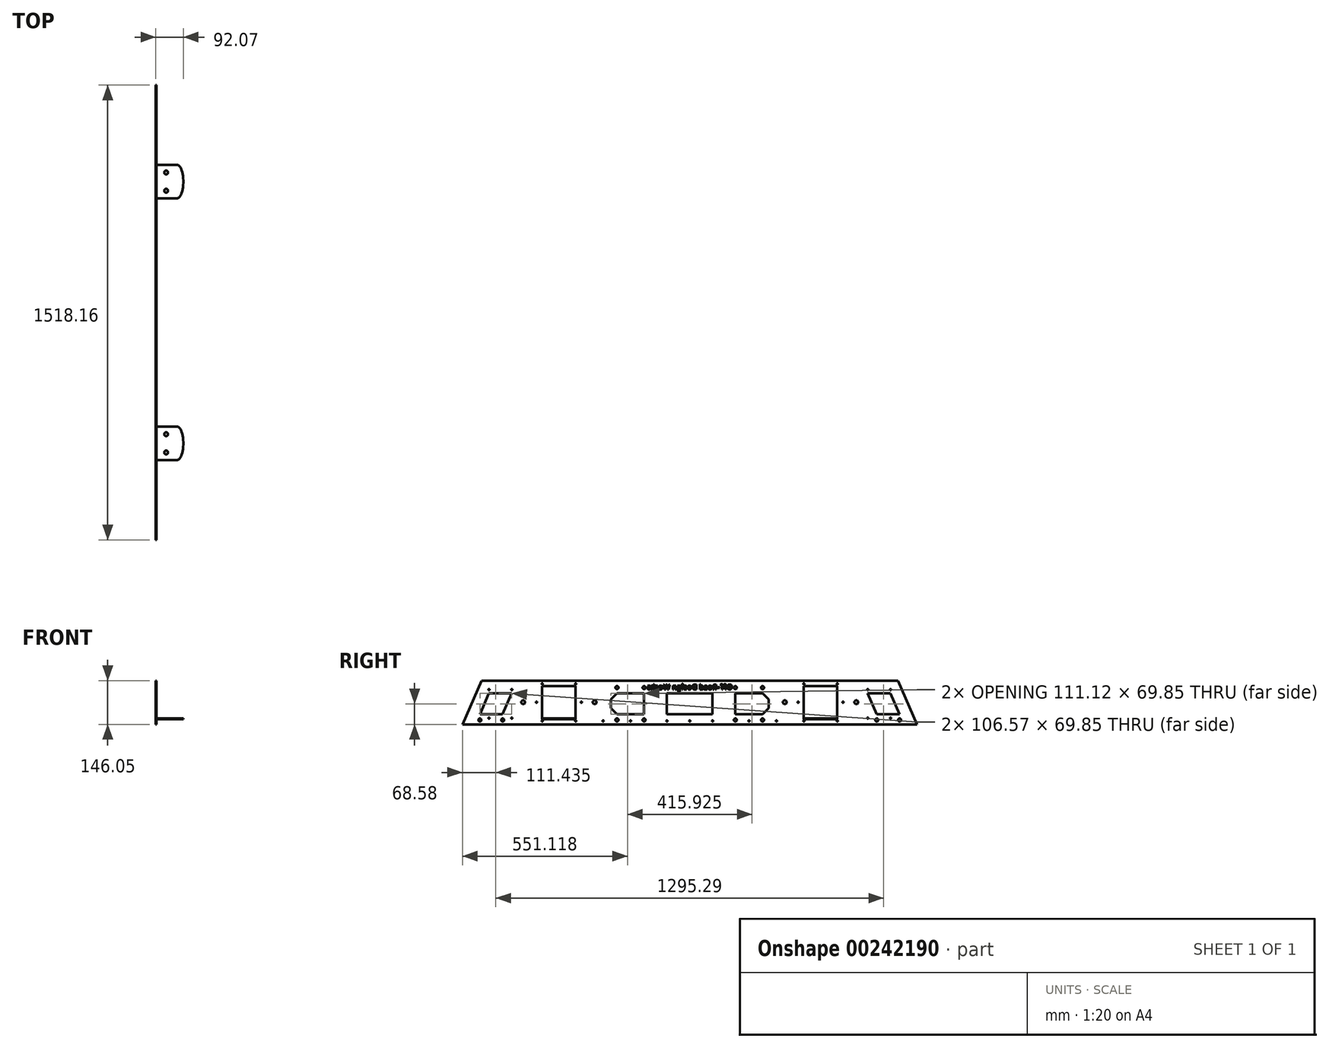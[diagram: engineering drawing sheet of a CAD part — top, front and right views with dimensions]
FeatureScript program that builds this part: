
annotation { "Feature Type Name" : "Feature", "Feature Type Description" : "" }
export const myFeature = defineFeature(function(context is Context, id is Id, definition is map)
    precondition{}
    {
        {
            var Q0;
            Q0=qCreatedBy(makeId("Right.planeOp"),FACE);
            var sketch = newSketch(context, id + "F0", { "sketchPlane" : qUnion([Q0])});
            skLineSegment(sketch, "E0", {"start": v(0, 0) * mm, "end": v(-759.08, 0) * mm});
            skLineSegment(sketch, "E1", {"start": v(-759.08, 0) * mm, "end": v(-695.58, 146.05) * mm});
            skLineSegment(sketch, "E2", {"start": v(-695.58, 146.05) * mm, "end": v(0, 146.05) * mm});
            skLineSegment(sketch, "E3", {"start": v(0, 0) * mm, "end": v(0, 460.36) * mm, "construction": true});
            skLineSegment(sketch, "E4.MirrorCS", {"start": v(695.58, 146.05) * mm, "end": v(0, 146.05) * mm});
            skLineSegment(sketch, "E5.MirrorCS", {"start": v(759.08, 0) * mm, "end": v(695.58, 146.05) * mm});
            skLineSegment(sketch, "E6.MirrorCS", {"start": v(0, 0) * mm, "end": v(759.08, 0) * mm});
            skSolve(sketch);
        }
        {
            var Q0;
            Q0=qSketchRegion(id+"F0",true);
            extrude(context, id + "F1", {"entities" : qUnion([Q0]), "oppositeDirection" : true, "depth" : 3.17 * mm});
        }
        {
            var Q0;
            Q0=makeQuery(id+"F1.opExtrude","CAP_FACE",FACE,{"disambiguationData":[OSD([sQuery(id+"F0.wireOp",EDGE,"E0"),sQuery(id+"F0.wireOp",EDGE,"E1"),sQuery(id+"F0.wireOp",EDGE,"E2"),sQuery(id+"F0.wireOp",EDGE,"E4.MirrorCS"),sQuery(id+"F0.wireOp",EDGE,"E5.MirrorCS"),sQuery(id+"F0.wireOp",EDGE,"E6.MirrorCS")])],"isStart":true});
            var sketch = newSketch(context, id + "F2", { "sketchPlane" : qUnion([Q0])});
            skLineSegment(sketch, "E7", {"start": v(0, 0) * mm, "end": v(0, 457.35) * mm, "construction": true});
            skLineSegment(sketch, "E8.bottom", {"start": v(-492.76, 127.5) * mm, "end": v(-381, 127.5) * mm});
            skLineSegment(sketch, "E8.top", {"start": v(-492.76, 20.32) * mm, "end": v(-381, 20.32) * mm});
            skLineSegment(sketch, "E8.left", {"start": v(-492.76, 127.5) * mm, "end": v(-492.76, 20.32) * mm});
            skLineSegment(sketch, "E8.right", {"start": v(-381, 127.5) * mm, "end": v(-381, 20.32) * mm});
            skLineSegment(sketch, "E9", {"start": v(-594.36, 103.5) * mm, "end": v(-670.56, 103.5) * mm});
            skLineSegment(sketch, "E10", {"start": v(-670.56, 103.5) * mm, "end": v(-700.93, 33.65) * mm});
            skLineSegment(sketch, "E11", {"start": v(-700.93, 33.65) * mm, "end": v(-624.73, 33.65) * mm});
            skLineSegment(sketch, "E12", {"start": v(-624.73, 33.65) * mm, "end": v(-594.36, 103.5) * mm});
            skArc(sketch, "E13.cCircle", {"start": v(-228.6, 103.5) * mm, "mid": v(-263.53, 68.58) * mm, "end": v(-228.6, 33.65) * mm, "construction": true});
            skLineSegment(sketch, "E13.0", {"start": v(-243.07, 103.5) * mm, "end": v(-214.13, 103.5) * mm});
            skLineSegment(sketch, "E13.4", {"start": v(-214.13, 33.65) * mm, "end": v(-243.07, 33.65) * mm});
            skLineSegment(sketch, "E13.5", {"start": v(-243.07, 33.65) * mm, "end": v(-263.53, 54.11) * mm});
            skLineSegment(sketch, "E13.6", {"start": v(-263.53, 54.11) * mm, "end": v(-263.53, 83.05) * mm});
            skLineSegment(sketch, "E13.7", {"start": v(-263.53, 83.05) * mm, "end": v(-243.07, 103.5) * mm});
            skPoint(sketch, "E13.0.midPoint", {"position": v(-228.6, 103.5) * mm});
            skLineSegment(sketch, "E14", {"start": v(-228.6, 33.65) * mm, "end": v(-152.4, 33.65) * mm});
            skLineSegment(sketch, "E15.MirrorCS", {"start": v(492.76, 127.5) * mm, "end": v(381, 127.5) * mm});
            skLineSegment(sketch, "E16.MirrorCS", {"start": v(492.76, 20.32) * mm, "end": v(381, 20.32) * mm});
            skLineSegment(sketch, "E17.MirrorCS", {"start": v(492.76, 127.5) * mm, "end": v(492.76, 20.32) * mm});
            skLineSegment(sketch, "E18.MirrorCS", {"start": v(381, 127.5) * mm, "end": v(381, 20.32) * mm});
            skLineSegment(sketch, "E19.MirrorCS", {"start": v(594.36, 103.5) * mm, "end": v(670.56, 103.5) * mm});
            skLineSegment(sketch, "E20.MirrorCS", {"start": v(670.56, 103.5) * mm, "end": v(700.93, 33.66) * mm});
            skLineSegment(sketch, "E21.MirrorCS", {"start": v(700.93, 33.65) * mm, "end": v(624.73, 33.65) * mm});
            skLineSegment(sketch, "E22.MirrorCS", {"start": v(624.73, 33.65) * mm, "end": v(594.36, 103.5) * mm});
            skLineSegment(sketch, "E23.MirrorCS", {"start": v(263.53, 54.11) * mm, "end": v(263.53, 83.05) * mm});
            skLineSegment(sketch, "E24.MirrorCS", {"start": v(263.53, 83.05) * mm, "end": v(243.07, 103.5) * mm});
            skArc(sketch, "E25.MirrorCS", {"start": v(228.6, 103.5) * mm, "mid": v(263.53, 68.58) * mm, "end": v(228.6, 33.65) * mm, "construction": true});
            skLineSegment(sketch, "E26.MirrorCS", {"start": v(243.07, 33.65) * mm, "end": v(263.53, 54.11) * mm});
            skLineSegment(sketch, "E27.MirrorCS", {"start": v(214.13, 33.65) * mm, "end": v(243.07, 33.65) * mm});
            skLineSegment(sketch, "E28.MirrorCS", {"start": v(243.07, 103.5) * mm, "end": v(214.13, 103.5) * mm});
            skLineSegment(sketch, "E29.MirrorCS", {"start": v(0, 103.5) * mm, "end": v(76.2, 103.5) * mm});
            skLineSegment(sketch, "E30.MirrorCS", {"start": v(228.6, 33.65) * mm, "end": v(152.4, 33.65) * mm});
            skLineSegment(sketch, "E31", {"start": v(-114.3, 103.5) * mm, "end": v(-114.3, -30.3) * mm, "construction": true});
            skLineSegment(sketch, "E32", {"start": v(-152.4, 103.5) * mm, "end": v(-152.4, 33.65) * mm});
            skLineSegment(sketch, "E33.MirrorCS", {"start": v(-76.2, 103.5) * mm, "end": v(-76.2, 33.65) * mm});
            skLineSegment(sketch, "E34.trimOffspring", {"start": v(-152.4, 103.5) * mm, "end": v(-228.6, 103.5) * mm});
            skPoint(sketch, "E35.start.orphan", {"position": v(0, 103.5) * mm});
            skLineSegment(sketch, "E36.trimOffspring", {"start": v(-76.2, 33.65) * mm, "end": v(0, 33.65) * mm});
            skLineSegment(sketch, "E37", {"start": v(-76.2, 103.5) * mm, "end": v(0, 103.5) * mm});
            skLineSegment(sketch, "E38", {"start": v(114.3, 103.5) * mm, "end": v(114.3, -63.26) * mm, "construction": true});
            skPoint(sketch, "E38.endSnap0", {"position": v(114.3, 103.5) * mm});
            skLineSegment(sketch, "E39", {"start": v(152.4, 103.5) * mm, "end": v(152.4, 33.65) * mm});
            skLineSegment(sketch, "E40.MirrorCS", {"start": v(76.2, 103.5) * mm, "end": v(76.2, 33.65) * mm});
            skLineSegment(sketch, "E41.trimOffspring", {"start": v(152.4, 103.5) * mm, "end": v(228.6, 103.5) * mm});
            skLineSegment(sketch, "E42.trimOffspring", {"start": v(76.2, 33.65) * mm, "end": v(0, 33.65) * mm});
            skSolve(sketch);
        }
        {
            var Q0;
            Q0=qSketchRegion(id+"F2",true);
            var Q1;
            Q1=makeQuery(id+"F1.opExtrude","CAP_FACE",FACE,{"disambiguationData":[OSD([sQuery(id+"F0.wireOp",EDGE,"E0"),sQuery(id+"F0.wireOp",EDGE,"E1"),sQuery(id+"F0.wireOp",EDGE,"E2"),sQuery(id+"F0.wireOp",EDGE,"E4.MirrorCS"),sQuery(id+"F0.wireOp",EDGE,"E5.MirrorCS"),sQuery(id+"F0.wireOp",EDGE,"E6.MirrorCS")])],"isStart":false});
            extrude(context, id + "F3", {"entities" : qUnion([Q0]), "operationType" : NewBodyOperationType.REMOVE, "endBound" : BoundingType.UP_TO_SURFACE, "oppositeDirection" : true, "endBoundEntityFace" : qUnion([Q1]), "depth" : 25.4 * mm});
        }
        {
            var Q0;
            Q0=makeQuery(id+"F1.opExtrude","CAP_FACE",FACE,{"disambiguationData":[OSD([sQuery(id+"F0.wireOp",EDGE,"E0"),sQuery(id+"F0.wireOp",EDGE,"E1"),sQuery(id+"F0.wireOp",EDGE,"E2"),sQuery(id+"F0.wireOp",EDGE,"E4.MirrorCS"),sQuery(id+"F0.wireOp",EDGE,"E5.MirrorCS"),sQuery(id+"F0.wireOp",EDGE,"E6.MirrorCS")])],"isStart":true});
            var sketch = newSketch(context, id + "F4", { "sketchPlane" : qUnion([Q0])});
            skCircle(sketch, "E43", {"center": v(-670.56, 116.2) * mm, "radius": 1.9 * mm});
            skCircle(sketch, "E44", {"center": v(-594.36, 116.2) * mm, "radius": 1.9 * mm});
            skCircle(sketch, "E45", {"center": v(-670.56, 20.95) * mm, "radius": 1.9 * mm});
            skCircle(sketch, "E46", {"center": v(-594.36, 20.95) * mm, "radius": 1.9 * mm});
            skCircle(sketch, "E47", {"center": v(-624.73, 14.6) * mm, "radius": 5.08 * mm});
            skCircle(sketch, "E48", {"center": v(-700.93, 14.6) * mm, "radius": 5.08 * mm});
            skCircle(sketch, "E49", {"center": v(-492.76, 135.13) * mm, "radius": 1.9 * mm});
            skCircle(sketch, "E50", {"center": v(-381, 135.13) * mm, "radius": 1.9 * mm});
            skLineSegment(sketch, "E51", {"start": v(-492.76, 73.91) * mm, "end": v(-416.14, 73.91) * mm, "construction": true});
            skCircle(sketch, "E52", {"center": v(-492.76, 11.43) * mm, "radius": 1.9 * mm});
            skCircle(sketch, "E53", {"center": v(-381, 11.43) * mm, "radius": 1.9 * mm});
            skCircle(sketch, "E54", {"center": v(-243.07, 14.6) * mm, "radius": 5.08 * mm});
            skCircle(sketch, "E55", {"center": v(-152.4, 14.6) * mm, "radius": 5.08 * mm});
            skLineSegment(sketch, "E56", {"start": v(-263.53, 68.58) * mm, "end": v(-277.88, 68.58) * mm, "construction": true});
            skCircle(sketch, "E57.MirrorC", {"center": v(-243.07, 122.56) * mm, "radius": 5.08 * mm});
            skCircle(sketch, "E58.MirrorC", {"center": v(-152.4, 122.56) * mm, "radius": 5.08 * mm});
            skLineSegment(sketch, "E59", {"start": v(0, 0) * mm, "end": v(0, -131.47) * mm, "construction": true});
            skCircle(sketch, "E60.MirrorC", {"center": v(152.4, 122.56) * mm, "radius": 5.08 * mm});
            skCircle(sketch, "E61.MirrorC", {"center": v(243.07, 122.56) * mm, "radius": 5.08 * mm});
            skCircle(sketch, "E62.MirrorC", {"center": v(243.07, 14.6) * mm, "radius": 5.08 * mm});
            skCircle(sketch, "E63.MirrorC", {"center": v(152.4, 14.6) * mm, "radius": 5.08 * mm});
            skCircle(sketch, "E64.MirrorC", {"center": v(381, 11.43) * mm, "radius": 1.9 * mm});
            skCircle(sketch, "E65.MirrorC", {"center": v(492.76, 11.43) * mm, "radius": 1.9 * mm});
            skCircle(sketch, "E66.MirrorC", {"center": v(492.76, 135.13) * mm, "radius": 1.9 * mm});
            skCircle(sketch, "E67.MirrorC", {"center": v(381, 135.13) * mm, "radius": 1.9 * mm});
            skCircle(sketch, "E68.MirrorC", {"center": v(594.36, 116.2) * mm, "radius": 1.9 * mm});
            skCircle(sketch, "E69.MirrorC", {"center": v(670.56, 116.2) * mm, "radius": 1.9 * mm});
            skCircle(sketch, "E70.MirrorC", {"center": v(670.56, 20.95) * mm, "radius": 1.9 * mm});
            skCircle(sketch, "E71.MirrorC", {"center": v(594.36, 20.95) * mm, "radius": 1.9 * mm});
            skCircle(sketch, "E72.MirrorC", {"center": v(624.73, 14.6) * mm, "radius": 5.08 * mm});
            skCircle(sketch, "E73.MirrorC", {"center": v(700.93, 14.6) * mm, "radius": 5.08 * mm});
            skCircle(sketch, "E74", {"center": v(-361.95, 73.91) * mm, "radius": 1.9 * mm});
            skPoint(sketch, "E74.centerSnap0", {"position": v(-381, 73.91) * mm});
            skCircle(sketch, "E75", {"center": v(-511.81, 73.91) * mm, "radius": 1.9 * mm});
            skCircle(sketch, "E76.MirrorC", {"center": v(361.95, 73.91) * mm, "radius": 1.9 * mm});
            skCircle(sketch, "E77.MirrorC", {"center": v(511.81, 73.91) * mm, "radius": 1.9 * mm});
            skCircle(sketch, "E78", {"center": v(-197.73, 11.43) * mm, "radius": 1.9 * mm});
            skPoint(sketch, "E78.centerSnap0", {"position": v(-197.73, 33.66) * mm});
            skCircle(sketch, "E79", {"center": v(-289.37, 11.43) * mm, "radius": 1.9 * mm});
            skCircle(sketch, "E80.MirrorC", {"center": v(197.73, 11.43) * mm, "radius": 1.9 * mm});
            skCircle(sketch, "E81.MirrorC", {"center": v(289.37, 11.43) * mm, "radius": 1.9 * mm});
            skCircle(sketch, "E82", {"center": v(-76.2, 11.43) * mm, "radius": 1.9 * mm});
            skCircle(sketch, "E83", {"center": v(0, 11.43) * mm, "radius": 1.9 * mm});
            skPoint(sketch, "E83.centerSnap0", {"position": v(0, 33.66) * mm});
            skCircle(sketch, "E84", {"center": v(76.2, 11.43) * mm, "radius": 1.9 * mm});
            skCircle(sketch, "E85", {"center": v(-317.5, 73.91) * mm, "radius": 6.35 * mm});
            skCircle(sketch, "E86", {"center": v(-556.26, 73.91) * mm, "radius": 6.35 * mm});
            skCircle(sketch, "E87.MirrorC", {"center": v(317.5, 73.91) * mm, "radius": 6.35 * mm});
            skCircle(sketch, "E88.MirrorC", {"center": v(556.26, 73.91) * mm, "radius": 6.35 * mm});
            skSolve(sketch);
        }
        {
            var Q0;
            Q0=qSketchRegion(id+"F4",true);
            var Q1;
            Q1=makeQuery(id+"F1.opExtrude","CAP_FACE",FACE,{"disambiguationData":[OSD([sQuery(id+"F0.wireOp",EDGE,"E0"),sQuery(id+"F0.wireOp",EDGE,"E1"),sQuery(id+"F0.wireOp",EDGE,"E2"),sQuery(id+"F0.wireOp",EDGE,"E4.MirrorCS"),sQuery(id+"F0.wireOp",EDGE,"E5.MirrorCS"),sQuery(id+"F0.wireOp",EDGE,"E6.MirrorCS")])],"isStart":false});
            extrude(context, id + "F5", {"entities" : qUnion([Q0]), "operationType" : NewBodyOperationType.REMOVE, "endBound" : BoundingType.UP_TO_SURFACE, "oppositeDirection" : true, "endBoundEntityFace" : qUnion([Q1]), "depth" : 25.4 * mm});
        }
        {
            var Q0;
            Q0=makeQuery(id+"F3.boolean.opBoolean","COPY",FACE,{"derivedFrom":makeQuery(id+"F3.opExtrude","SWEPT_FACE",FACE,{"disambiguationData":[OSD([sQuery(id+"F2.wireOp",EDGE,"E8.top")])]})});
            var sketch = newSketch(context, id + "F6", { "sketchPlane" : qUnion([Q0])});
            skLineSegment(sketch, "E89", {"start": v(-3.18, -436.88) * mm, "end": v(-45.3, -436.88) * mm, "construction": true});
            skLineSegment(sketch, "E90", {"start": v(-3.18, -492.76) * mm, "end": v(-71.76, -492.76) * mm});
            skLineSegment(sketch, "E91.MirrorCS", {"start": v(-3.18, -381) * mm, "end": v(-71.76, -381) * mm});
            skEllipticalArc(sketch, "E92", {});
            skLineSegment(sketch, "E93", {"start": v(-3.18, -492.76) * mm, "end": v(-3.18, -381) * mm});
            skCircle(sketch, "E94", {"center": v(-34.93, -467.36) * mm, "radius": 6.35 * mm});
            skCircle(sketch, "E95.MirrorC", {"center": v(-34.93, -406.4) * mm, "radius": 6.35 * mm});
            skLineSegment(sketch, "E96", {"start": v(0, 0) * mm, "end": v(-238.43, 0) * mm, "construction": true});
            skLineSegment(sketch, "E97.MirrorCS", {"start": v(-3.18, 381) * mm, "end": v(-71.76, 381) * mm});
            skEllipticalArc(sketch, "E98.MirrorCS", {});
            skCircle(sketch, "E99.MirrorC", {"center": v(-34.93, 406.4) * mm, "radius": 6.35 * mm});
            skCircle(sketch, "E100.MirrorC", {"center": v(-34.93, 467.36) * mm, "radius": 6.35 * mm});
            skLineSegment(sketch, "E101.MirrorCS", {"start": v(-3.18, 492.76) * mm, "end": v(-71.76, 492.76) * mm});
            skLineSegment(sketch, "E102.MirrorCS", {"start": v(-3.18, 492.76) * mm, "end": v(-3.18, 381) * mm});
            const initialGuessF6  = {"E92": [-0.071755, -0.43688, 0, -1, 0.05588, 0.02032, 3.141592653589793, 0], "E98.MirrorCS": [-0.071755, 0.43688, 0, 1, 0.05588, 0.02032, 0, 3.141592653589793]};
            skSetInitialGuess(sketch, initialGuessF6);
            skSolve(sketch);
        }
        {
            var Q0;
            Q0=qSketchRegion(id+"F6",true);
            extrude(context, id + "F7", {"entities" : qUnion([Q0]), "operationType" : NewBodyOperationType.ADD, "oppositeDirection" : true, "depth" : 3.17 * mm});
        }
        {
            var Q0;
            Q0=makeQuery(id+"F1.opExtrude","SWEPT_BODY",BODY,{"disambiguationData":[OSD([sQuery(id+"F0.wireOp",EDGE,"E0"),sQuery(id+"F0.wireOp",EDGE,"E1"),sQuery(id+"F0.wireOp",EDGE,"E2"),sQuery(id+"F0.wireOp",EDGE,"E4.MirrorCS"),sQuery(id+"F0.wireOp",EDGE,"E5.MirrorCS"),sQuery(id+"F0.wireOp",EDGE,"E6.MirrorCS")])]});
            var Q1;
            Q1=qCreatedBy(makeId("Right.planeOp"),FACE);
            mirror(context, id + "F8", {"entities" : qUnion([Q0]), "mirrorPlane" : qUnion([Q1])});
        }
        {
            var Q0;
            Q0=makeQuery(id+"F1.opExtrude","SWEPT_BODY",BODY,{"disambiguationData":[OSD([sQuery(id+"F0.wireOp",EDGE,"E0"),sQuery(id+"F0.wireOp",EDGE,"E1"),sQuery(id+"F0.wireOp",EDGE,"E2"),sQuery(id+"F0.wireOp",EDGE,"E4.MirrorCS"),sQuery(id+"F0.wireOp",EDGE,"E5.MirrorCS"),sQuery(id+"F0.wireOp",EDGE,"E6.MirrorCS")])]});
            deleteBodies(context, id + "F9", {"entities" : qUnion([Q0])});
        }
        {
            var Q0;
            Q0=makeQuery(id+"F8.opPattern","COPY",FACE,{"derivedFrom":makeQuery(id+"F1.opExtrude","CAP_FACE",FACE,{"disambiguationData":[OSD([sQuery(id+"F0.wireOp",EDGE,"E0"),sQuery(id+"F0.wireOp",EDGE,"E1"),sQuery(id+"F0.wireOp",EDGE,"E2"),sQuery(id+"F0.wireOp",EDGE,"E4.MirrorCS"),sQuery(id+"F0.wireOp",EDGE,"E5.MirrorCS"),sQuery(id+"F0.wireOp",EDGE,"E6.MirrorCS")])],"isStart":true}),"instanceName":"1"});
            var sketch = newSketch(context, id + "F10", { "sketchPlane" : qUnion([Q0])});
            skText(sketch, "E103", { "text": "Off-Road Design Works", "fontName": "AllertaStencil-Regular.ttf"});
            skLineSegment(sketch, "E104", {"start": v(0, 116.2) * mm, "end": v(0, 0) * mm, "construction": true});
            const initialGuessF10  = {"E103": [-0.14224, 0.1162, 1, 0, 0.01718]};
            skSetInitialGuess(sketch, initialGuessF10);
            skSolve(sketch);
        }
        {
            var Q0;
            Q0 = qSketchRegion(id + "F10", true);
            var Q1;
            Q1=makeQuery(id+"F8.opPattern","COPY",FACE,{"derivedFrom":makeQuery(id+"F1.opExtrude","CAP_FACE",FACE,{"disambiguationData":[OSD([sQuery(id+"F0.wireOp",EDGE,"E0"),sQuery(id+"F0.wireOp",EDGE,"E1"),sQuery(id+"F0.wireOp",EDGE,"E2"),sQuery(id+"F0.wireOp",EDGE,"E4.MirrorCS"),sQuery(id+"F0.wireOp",EDGE,"E5.MirrorCS"),sQuery(id+"F0.wireOp",EDGE,"E6.MirrorCS")])],"isStart":false}),"instanceName":"1"});
            extrude(context, id + "F11", {"entities" : qUnion([Q0]), "operationType" : NewBodyOperationType.REMOVE, "endBound" : BoundingType.UP_TO_SURFACE, "oppositeDirection" : true, "endBoundEntityFace" : qUnion([Q1]), "depth" : 25.4 * mm});
        }
    });
